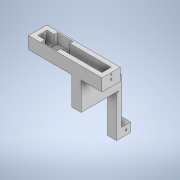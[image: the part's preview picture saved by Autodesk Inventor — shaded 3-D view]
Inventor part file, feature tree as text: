
AUTODESK INVENTOR PART (.ipt)
format: ipt  version: 2020 (Build 240168000, 168)  size: 251,392 bytes
history: native  units: in
note: dims shown in document units (in); Inventor stores cm internally (conversion verified against a paired STEP export)
features: extrude x14, sketch x14, fillet x1
ambient origin geometry x8: Origin, YZ Plane, XZ Plane, XY Plane, X Axis, Y Axis, Z Axis, Center Point
bodies: Solid1 (feature_tree)
feature tree (29):
  extrude  "Extrusion1"  Depth=1.5in
  extrude  "Extrusion2"  Depth=0.375in
  extrude  "Extrusion3"  Depth=0.375in
  extrude  "Extrusion4"  Depth=0.75in TaperAngle=0.0deg
  extrude  "Extrusion5"  Depth=7.5625in TaperAngle=0.0deg
  extrude  "Extrusion6"  Depth=0.8in
  extrude  "Extrusion7"  Depth=0.77in
  extrude  "Extrusion8"  Depth=0.141in
  fillet  "Fillet1"  Radius=0.141in
  extrude  "Extrusion9"  Depth=0.25in
  extrude  "Extrusion10"  Depth=1.8in TaperAngle=0.0deg
  extrude  "Extrusion13"  Depth=0.0625in
  extrude  "Extrusion14"  Depth=0.25in TaperAngle=0.0deg
  extrude  "Extrusion15"  Depth=0.75in
  extrude  "Extrusion16"  Depth=0.75in TaperAngle=0.0deg
  sketch  "Sketch1"  dims[d0=6.0in d1=1.5in]
  sketch  "Sketch3"  dims[d2=1.0in d3=0.0in d4=0.375in]
  sketch  "Sketch4"  dims[d5=0.375in d6=0.375in]
  sketch  "Sketch5"  dims[d7=0.375in d8=0.75in d9=0.0in]
  sketch  "Sketch6"  dims[d13=7.5625in d14=0.0in d20=7.5625in d21=0.0in]
  sketch  "Sketch7"  dims[d22=0.8in d23=0.0in d24=0.141in]
  sketch  "Sketch8"  dims[d25=0.141in d31=0.77in]
  sketch  "Sketch9"  dims[d32=0.141in d33=0.141in d34=0.141in]
  sketch  "Sketch10"  dims[d35=0.141in d36=0.25in]
  sketch  "Sketch11"  dims[d37=2.3in d38=0.0in d39=1.8in d40=0.0in]
  sketch  "Sketch14"  dims[d41=3.0in d42=0.0in d43=0.0625in]
  sketch  "Sketch15"  dims[d44=0.25in d45=0.0in d46=0.5in d47=0.0in]
  sketch  "Sketch16"  dims[d55=0.446in d56=0.0in d57=0.75in]
  sketch  "Sketch17"  dims[d58=0.75in d59=0.75in d60=0.0in d61=0.141in d62=1.5625in d63=0.0in d64=0.156in d65=0.0in]
